# Revit family: DOC30M977D_Revit
name_source: partatom
category: Specialty Equipment
revit_build: Autodesk Revit MEP 2014 (Build: 20130308_1515(x64)
units: mm (PartAtom-declared; Revit-internal decimal feet)

## types (1)
- DOC30M977D
    BAKE ELEMENT = 3,000W - 8 PASS
    BROIL ELEMENT = 4,400W - 10 PASS
    CHILD LOCK = YES
    CIRCUIT BREAKER (A) = 40
    CLEANING TYPE = SELF CLEAN GREENCLEAN™
    CLOCK = YES (12 HR/24 HR)
    CLOCK YES = (12 HR/24 HR)
    CONTROLS = 7” LCD
    CONVECTION ELEMENT = 1,300W (EACH - 2,600W TOTAL)
    CONVECTION TYPE = FOUR PART DUAL PURE CONVECTION WITH MESH FILTER
    COOKIE SHEETS (SET OF 3) = SKU - ACSM303
    COOKING MODES LOWER CAVITY = BAKE - BROIL - CONVECTION BAKE - CONVECTION ROAST - CONVECTION BROIL - FOUR PART PURE CONVECTION - PURE CONVECTION SEAR - STEAM BAKE - STEAM ROAST
    COOKING MODES UPPER CAVITY = BROIL - CONVECTION SEAR (POWER CONVECTION) - SPEED CONVECTION SEAR - SPEED BROIL
    DELAY START = YES
    DEMO MODE = YES
    Depth = 23 1/8"
    Description = 30-INCH COMBI WALL OVEN MODERNIST COLLECTION
    Door = Stainless Steel
    ENERGY SAVING = YES
    ENERGY SOURCE = ELECTRIC
    FREQUENCY (HZ) = 60
    Front Door = Glass
    Handle = Stainless Steel
    Height = 43 3/8"
    INSTALLATION = FLUSH
    KITCHEN TIMER = YES
    LAMP ON/OFF = YES
    LANGUAGE OPTIONS = YES
    LIGHTING = BRIGHTVUE™ AND RADIANTVUE™
    LIMITED, PARTS AND LABOR = 1 YEAR
    Manufacturer = Dacor
    Model = DOC30M977D
    OPTIONS = YES
    OVEN COLORS = SILVER STAINLESS STEEL GRAPHITE STAINLESS STEEL
    OVEN TYPE = COMBINATION
    POWER LEVEL = 950W
    SABBATH MODE = YES
    SOFT CLOSE DOOR (OVEN) = SOFTSHUT™
    SOUND = YES
    STEAM HEATER = 500W
    Support = Plastic-Black
    TYPE = COMBINATION MICROWAVE/OVEN
    Unit = Stainless Steel
    VOLTS (V) = 240 / 208
    WI FI = YES (REMOTE ENABLED)
    WI FI ON/OFF = YES
    Width = 29 3/4"

## geometry (parser evidence)
native form markers: Blend x4, Sweep x1
no freeform markers — native parametric forms only
